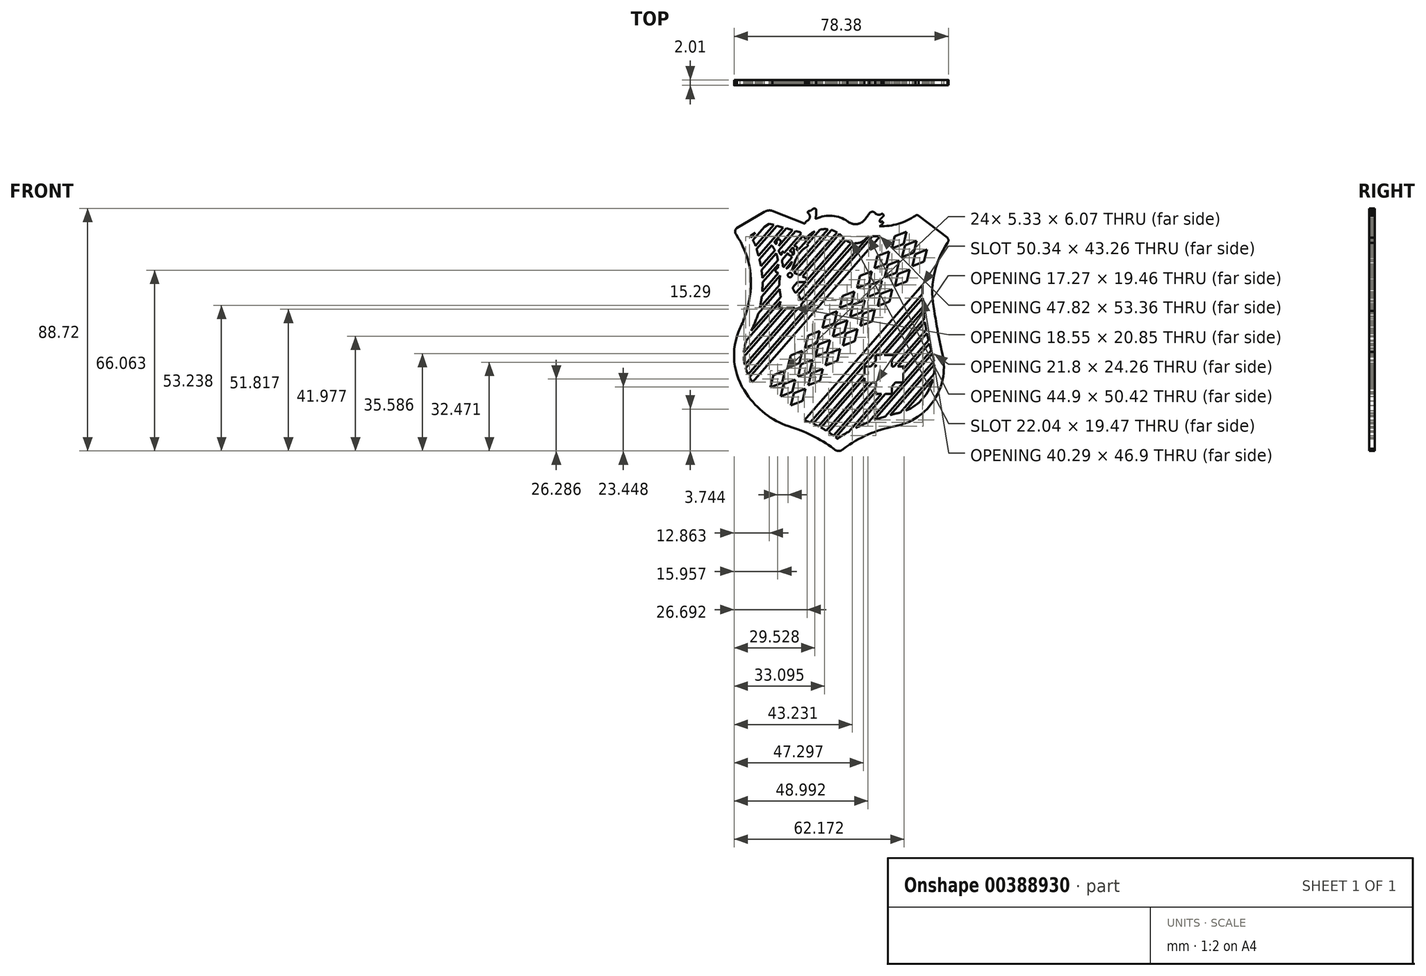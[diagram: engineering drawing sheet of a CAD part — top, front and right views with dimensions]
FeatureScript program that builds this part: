
annotation { "Feature Type Name" : "Feature", "Feature Type Description" : "" }
export const myFeature = defineFeature(function(context is Context, id is Id, definition is map)
    precondition{}
    {
        {
            var Q0;
            Q0=qCreatedBy(makeId("Front.planeOp"),FACE);
            var sketch = newSketch(context, id + "F0", { "sketchPlane" : qUnion([Q0])});
            skLineSegment(sketch, "E0", {"start": v(5.3, 4.8) * mm, "end": v(-12.55, -15.64) * mm});
            skLineSegment(sketch, "E1", {"start": v(11.24, -1.99) * mm, "end": v(-5.34, -20.97) * mm});
            skArc(sketch, "E2", {"start": v(-0.72, -23.55) * mm, "mid": v(-0.82, -23.46) * mm, "end": v(-0.92, -23.38) * mm});
            skArc(sketch, "E3", {"start": v(7.71, -19.98) * mm, "mid": v(7.22, -20.1) * mm, "end": v(6.72, -20.22) * mm});
            skArc(sketch, "E4", {"start": v(7.71, -19.98) * mm, "mid": v(7.92, -19.94) * mm, "end": v(8.13, -19.88) * mm});
            skArc(sketch, "E5", {"start": v(11.24, -1.99) * mm, "mid": v(11.23, -2.63) * mm, "end": v(11.23, -3.27) * mm});
            skArc(sketch, "E6", {"start": v(-11.88, 2.51) * mm, "mid": v(-11.95, 2.77) * mm, "end": v(-12.02, 3.03) * mm});
            skLineSegment(sketch, "E7", {"start": v(-10.25, 6.58) * mm, "end": v(-9.6, 6.4) * mm});
            skLineSegment(sketch, "E8", {"start": v(-5.95, 5.4) * mm, "end": v(-5.78, 5.19) * mm});
            skArc(sketch, "E9", {"start": v(0, 4.79) * mm, "mid": v(-0.2, 4.97) * mm, "end": v(-0.4, 5.14) * mm});
            skArc(sketch, "E10", {"start": v(0, 4.79) * mm, "mid": v(0.09, 4.66) * mm, "end": v(0.18, 4.54) * mm});
            skLineSegment(sketch, "E11", {"start": v(3.54, 4.79) * mm, "end": v(3.66, 4.79) * mm});
            skLineSegment(sketch, "E12", {"start": v(-10.08, -16.36) * mm, "end": v(-9.67, -14.67) * mm});
            skLineSegment(sketch, "E13", {"start": v(-9.67, -14.67) * mm, "end": v(-8.04, -14.03) * mm});
            skLineSegment(sketch, "E14", {"start": v(-8.45, -15.72) * mm, "end": v(-8.04, -14.03) * mm});
            skLineSegment(sketch, "E15", {"start": v(-10.08, -16.36) * mm, "end": v(-8.45, -15.72) * mm});
            skLineSegment(sketch, "E16", {"start": v(-7.65, -13.58) * mm, "end": v(-7.24, -11.89) * mm});
            skLineSegment(sketch, "E17", {"start": v(-7.24, -11.89) * mm, "end": v(-5.6, -11.25) * mm});
            skLineSegment(sketch, "E18", {"start": v(-6.02, -12.94) * mm, "end": v(-5.6, -11.25) * mm});
            skLineSegment(sketch, "E19", {"start": v(-7.65, -13.58) * mm, "end": v(-6.02, -12.94) * mm});
            skLineSegment(sketch, "E20", {"start": v(-5.22, -10.8) * mm, "end": v(-4.8, -9.1) * mm});
            skLineSegment(sketch, "E21", {"start": v(-4.8, -9.1) * mm, "end": v(-3.18, -8.47) * mm});
            skLineSegment(sketch, "E22", {"start": v(-3.58, -10.16) * mm, "end": v(-3.18, -8.47) * mm});
            skLineSegment(sketch, "E23", {"start": v(-5.22, -10.8) * mm, "end": v(-3.58, -10.16) * mm});
            skLineSegment(sketch, "E24", {"start": v(-2.79, -8) * mm, "end": v(-2.38, -6.32) * mm});
            skLineSegment(sketch, "E25", {"start": v(-2.38, -6.32) * mm, "end": v(-0.75, -5.68) * mm});
            skLineSegment(sketch, "E26", {"start": v(-1.15, -7.37) * mm, "end": v(-0.75, -5.68) * mm});
            skLineSegment(sketch, "E27", {"start": v(-2.79, -8) * mm, "end": v(-1.15, -7.37) * mm});
            skLineSegment(sketch, "E28", {"start": v(-0.36, -5.23) * mm, "end": v(0.05, -3.54) * mm});
            skLineSegment(sketch, "E29", {"start": v(0.05, -3.54) * mm, "end": v(1.69, -2.9) * mm});
            skLineSegment(sketch, "E30", {"start": v(1.28, -4.6) * mm, "end": v(1.69, -2.9) * mm});
            skLineSegment(sketch, "E31", {"start": v(-0.36, -5.23) * mm, "end": v(1.28, -4.6) * mm});
            skLineSegment(sketch, "E32", {"start": v(2.08, -2.44) * mm, "end": v(2.48, -0.75) * mm});
            skLineSegment(sketch, "E33", {"start": v(2.48, -0.75) * mm, "end": v(4.12, -0.12) * mm});
            skLineSegment(sketch, "E34", {"start": v(3.7, -1.8) * mm, "end": v(4.12, -0.12) * mm});
            skLineSegment(sketch, "E35", {"start": v(2.08, -2.44) * mm, "end": v(3.7, -1.8) * mm});
            skLineSegment(sketch, "E36", {"start": v(4.5, 0.34) * mm, "end": v(4.91, 2.03) * mm});
            skLineSegment(sketch, "E37", {"start": v(4.91, 2.03) * mm, "end": v(6.55, 2.67) * mm});
            skLineSegment(sketch, "E38", {"start": v(6.14, 0.98) * mm, "end": v(6.55, 2.67) * mm});
            skLineSegment(sketch, "E39", {"start": v(4.5, 0.34) * mm, "end": v(6.14, 0.98) * mm});
            skLineSegment(sketch, "E40", {"start": v(6.94, 3.12) * mm, "end": v(7.35, 4.81) * mm});
            skLineSegment(sketch, "E41", {"start": v(7.35, 4.81) * mm, "end": v(8.98, 5.45) * mm});
            skLineSegment(sketch, "E42", {"start": v(8.57, 3.76) * mm, "end": v(8.98, 5.45) * mm});
            skLineSegment(sketch, "E43", {"start": v(6.94, 3.12) * mm, "end": v(8.57, 3.76) * mm});
            skLineSegment(sketch, "E44", {"start": v(-8.64, -17.61) * mm, "end": v(-8.24, -15.92) * mm});
            skLineSegment(sketch, "E45", {"start": v(-8.24, -15.92) * mm, "end": v(-6.6, -15.29) * mm});
            skLineSegment(sketch, "E46", {"start": v(-7.01, -16.98) * mm, "end": v(-6.6, -15.29) * mm});
            skLineSegment(sketch, "E47", {"start": v(-8.64, -17.61) * mm, "end": v(-7.01, -16.98) * mm});
            skLineSegment(sketch, "E48", {"start": v(-6.21, -14.83) * mm, "end": v(-5.8, -13.14) * mm});
            skLineSegment(sketch, "E49", {"start": v(-5.8, -13.14) * mm, "end": v(-4.17, -12.5) * mm});
            skLineSegment(sketch, "E50", {"start": v(-4.58, -14.2) * mm, "end": v(-4.17, -12.5) * mm});
            skLineSegment(sketch, "E51", {"start": v(-6.21, -14.83) * mm, "end": v(-4.58, -14.2) * mm});
            skLineSegment(sketch, "E52", {"start": v(-3.78, -12.04) * mm, "end": v(-3.37, -10.36) * mm});
            skLineSegment(sketch, "E53", {"start": v(-3.37, -10.36) * mm, "end": v(-1.74, -9.72) * mm});
            skLineSegment(sketch, "E54", {"start": v(-2.15, -11.4) * mm, "end": v(-1.74, -9.72) * mm});
            skLineSegment(sketch, "E55", {"start": v(-3.78, -12.04) * mm, "end": v(-2.15, -11.4) * mm});
            skLineSegment(sketch, "E56", {"start": v(-1.35, -9.26) * mm, "end": v(-0.94, -7.57) * mm});
            skLineSegment(sketch, "E57", {"start": v(-0.94, -7.57) * mm, "end": v(0.69, -6.94) * mm});
            skLineSegment(sketch, "E58", {"start": v(0.28, -8.63) * mm, "end": v(0.69, -6.94) * mm});
            skLineSegment(sketch, "E59", {"start": v(-1.35, -9.26) * mm, "end": v(0.28, -8.63) * mm});
            skLineSegment(sketch, "E60", {"start": v(1.08, -6.48) * mm, "end": v(1.49, -4.79) * mm});
            skLineSegment(sketch, "E61", {"start": v(1.49, -4.79) * mm, "end": v(3.12, -4.15) * mm});
            skLineSegment(sketch, "E62", {"start": v(2.71, -5.84) * mm, "end": v(3.12, -4.15) * mm});
            skLineSegment(sketch, "E63", {"start": v(1.08, -6.48) * mm, "end": v(2.71, -5.84) * mm});
            skLineSegment(sketch, "E64", {"start": v(3.5, -3.7) * mm, "end": v(3.92, -2) * mm});
            skLineSegment(sketch, "E65", {"start": v(3.92, -2) * mm, "end": v(5.55, -1.37) * mm});
            skLineSegment(sketch, "E66", {"start": v(5.14, -3.06) * mm, "end": v(5.55, -1.37) * mm});
            skLineSegment(sketch, "E67", {"start": v(3.5, -3.7) * mm, "end": v(5.14, -3.06) * mm});
            skLineSegment(sketch, "E68", {"start": v(5.94, -0.91) * mm, "end": v(6.35, 0.78) * mm});
            skLineSegment(sketch, "E69", {"start": v(6.35, 0.78) * mm, "end": v(7.98, 1.41) * mm});
            skLineSegment(sketch, "E70", {"start": v(7.57, -0.28) * mm, "end": v(7.98, 1.41) * mm});
            skLineSegment(sketch, "E71", {"start": v(5.94, -0.91) * mm, "end": v(7.57, -0.28) * mm});
            skLineSegment(sketch, "E72", {"start": v(8.37, 1.87) * mm, "end": v(8.78, 3.56) * mm});
            skLineSegment(sketch, "E73", {"start": v(8.78, 3.56) * mm, "end": v(10.41, 4.2) * mm});
            skLineSegment(sketch, "E74", {"start": v(10, 2.5) * mm, "end": v(10.41, 4.2) * mm});
            skLineSegment(sketch, "E75", {"start": v(8.37, 1.87) * mm, "end": v(10, 2.5) * mm});
            skLineSegment(sketch, "E76", {"start": v(-7.21, -18.86) * mm, "end": v(-6.8, -17.17) * mm});
            skLineSegment(sketch, "E77", {"start": v(-6.8, -17.17) * mm, "end": v(-5.17, -16.54) * mm});
            skLineSegment(sketch, "E78", {"start": v(-5.58, -18.23) * mm, "end": v(-5.17, -16.54) * mm});
            skLineSegment(sketch, "E79", {"start": v(-7.21, -18.86) * mm, "end": v(-5.58, -18.23) * mm});
            skLineSegment(sketch, "E80", {"start": v(-4.78, -16.08) * mm, "end": v(-4.37, -14.4) * mm});
            skLineSegment(sketch, "E81", {"start": v(-4.37, -14.4) * mm, "end": v(-2.74, -13.76) * mm});
            skLineSegment(sketch, "E82", {"start": v(-3.15, -15.45) * mm, "end": v(-2.74, -13.76) * mm});
            skLineSegment(sketch, "E83", {"start": v(-4.78, -16.08) * mm, "end": v(-3.15, -15.45) * mm});
            skLineSegment(sketch, "E84", {"start": v(-2.35, -13.3) * mm, "end": v(-1.94, -11.6) * mm});
            skLineSegment(sketch, "E85", {"start": v(-1.94, -11.6) * mm, "end": v(-0.3, -10.97) * mm});
            skLineSegment(sketch, "E86", {"start": v(-0.72, -12.66) * mm, "end": v(-0.3, -10.97) * mm});
            skLineSegment(sketch, "E87", {"start": v(-2.35, -13.3) * mm, "end": v(-0.72, -12.66) * mm});
            skLineSegment(sketch, "E88", {"start": v(0.08, -10.51) * mm, "end": v(0.5, -8.82) * mm});
            skLineSegment(sketch, "E89", {"start": v(0.5, -8.82) * mm, "end": v(2.12, -8.19) * mm});
            skLineSegment(sketch, "E90", {"start": v(1.72, -9.88) * mm, "end": v(2.12, -8.19) * mm});
            skLineSegment(sketch, "E91", {"start": v(0.08, -10.51) * mm, "end": v(1.72, -9.88) * mm});
            skLineSegment(sketch, "E92", {"start": v(2.51, -7.73) * mm, "end": v(2.92, -6.04) * mm});
            skLineSegment(sketch, "E93", {"start": v(2.92, -6.04) * mm, "end": v(4.55, -5.4) * mm});
            skLineSegment(sketch, "E94", {"start": v(4.15, -7.1) * mm, "end": v(4.55, -5.4) * mm});
            skLineSegment(sketch, "E95", {"start": v(2.51, -7.73) * mm, "end": v(4.15, -7.1) * mm});
            skLineSegment(sketch, "E96", {"start": v(4.94, -4.95) * mm, "end": v(5.35, -3.26) * mm});
            skLineSegment(sketch, "E97", {"start": v(5.35, -3.26) * mm, "end": v(6.99, -2.62) * mm});
            skLineSegment(sketch, "E98", {"start": v(6.58, -4.31) * mm, "end": v(6.99, -2.62) * mm});
            skLineSegment(sketch, "E99", {"start": v(4.94, -4.95) * mm, "end": v(6.58, -4.31) * mm});
            skLineSegment(sketch, "E100", {"start": v(7.37, -2.16) * mm, "end": v(7.78, -0.47) * mm});
            skLineSegment(sketch, "E101", {"start": v(7.78, -0.47) * mm, "end": v(9.42, 0.16) * mm});
            skLineSegment(sketch, "E102", {"start": v(9, -1.53) * mm, "end": v(9.42, 0.16) * mm});
            skLineSegment(sketch, "E103", {"start": v(7.37, -2.16) * mm, "end": v(9, -1.53) * mm});
            skLineSegment(sketch, "E104", {"start": v(9.8, 0.62) * mm, "end": v(10.21, 2.3) * mm});
            skLineSegment(sketch, "E105", {"start": v(10.21, 2.3) * mm, "end": v(11.85, 2.94) * mm});
            skLineSegment(sketch, "E106", {"start": v(11.44, 1.25) * mm, "end": v(11.85, 2.94) * mm});
            skLineSegment(sketch, "E107", {"start": v(9.8, 0.62) * mm, "end": v(11.44, 1.25) * mm});
            skLineSegment(sketch, "E108", {"start": v(-4.5, -21.28) * mm, "end": v(11.23, -3.27) * mm});
            skLineSegment(sketch, "E109", {"start": v(11.25, -3.84) * mm, "end": v(-4.12, -21.44) * mm});
            skLineSegment(sketch, "E110", {"start": v(-1.92, -22.65) * mm, "end": v(4.17, -15.68) * mm});
            skLineSegment(sketch, "E111", {"start": v(3.69, -21.23) * mm, "end": v(8.54, -15.68) * mm});
            skLineSegment(sketch, "E112", {"start": v(4.47, -20.93) * mm, "end": v(12.59, -11.64) * mm});
            skLineSegment(sketch, "E113", {"start": v(6.03, -20.42) * mm, "end": v(12.82, -12.64) * mm});
            skLineSegment(sketch, "E114", {"start": v(6.72, -20.22) * mm, "end": v(12.88, -13.17) * mm});
            skLineSegment(sketch, "E115", {"start": v(8.13, -19.88) * mm, "end": v(12.84, -14.49) * mm});
            skLineSegment(sketch, "E116", {"start": v(8.87, -19.63) * mm, "end": v(12.69, -15.26) * mm});
            skArc(sketch, "E117", {"start": v(-4.5, -21.28) * mm, "mid": v(-4.92, -21.12) * mm, "end": v(-5.34, -20.97) * mm});
            skArc(sketch, "E118", {"start": v(-3.34, -21.81) * mm, "mid": v(-3.73, -21.62) * mm, "end": v(-4.12, -21.44) * mm});
            skArc(sketch, "E119", {"start": v(-2.25, -22.43) * mm, "mid": v(-2.61, -22.21) * mm, "end": v(-2.98, -22) * mm});
            skArc(sketch, "E120", {"start": v(-1.23, -23.14) * mm, "mid": v(-1.57, -22.89) * mm, "end": v(-1.92, -22.65) * mm});
            skArc(sketch, "E121", {"start": v(0.9, -22.57) * mm, "mid": v(0.08, -23.04) * mm, "end": v(-0.72, -23.55) * mm});
            skArc(sketch, "E122", {"start": v(3.69, -21.23) * mm, "mid": v(2.76, -21.63) * mm, "end": v(1.86, -22.06) * mm});
            skArc(sketch, "E123", {"start": v(8.87, -19.63) * mm, "mid": v(11.3, -17.9) * mm, "end": v(12.69, -15.26) * mm});
            skArc(sketch, "E124", {"start": v(12.84, -14.49) * mm, "mid": v(12.9, -13.83) * mm, "end": v(12.88, -13.17) * mm});
            skLineSegment(sketch, "E125", {"start": v(12.88, -13.17) * mm, "end": v(12.88, -13.17) * mm});
            skArc(sketch, "E126", {"start": v(12.19, -10.23) * mm, "mid": v(12.32, -10.72) * mm, "end": v(12.45, -11.2) * mm});
            skLineSegment(sketch, "E127", {"start": v(11.84, -8.76) * mm, "end": v(11.84, -8.76) * mm});
            skLineSegment(sketch, "E128", {"start": v(11.75, -8.27) * mm, "end": v(11.75, -8.27) * mm});
            skArc(sketch, "E129", {"start": v(11.57, -7.21) * mm, "mid": v(11.65, -7.75) * mm, "end": v(11.75, -8.27) * mm});
            skArc(sketch, "E130", {"start": v(11.36, -5.58) * mm, "mid": v(11.42, -6.14) * mm, "end": v(11.5, -6.7) * mm});
            skArc(sketch, "E131", {"start": v(11.25, -3.84) * mm, "mid": v(11.28, -4.44) * mm, "end": v(11.32, -5.03) * mm});
            skArc(sketch, "E132", {"start": v(11.84, -8.76) * mm, "mid": v(11.95, -9.27) * mm, "end": v(12.07, -9.77) * mm});
            skLineSegment(sketch, "E133.bottom", {"start": v(3.1, -13.45) * mm, "end": v(3.96, -13.45) * mm});
            skLineSegment(sketch, "E133.top", {"start": v(3.1, -15.68) * mm, "end": v(3.65, -15.68) * mm});
            skLineSegment(sketch, "E133.left", {"start": v(3.1, -13.45) * mm, "end": v(3.1, -14.45) * mm});
            skLineSegment(sketch, "E134.bottom", {"start": v(6.93, -11.85) * mm, "end": v(6.93, -11.92) * mm});
            skLineSegment(sketch, "E134.right", {"start": v(6.93, -17.3) * mm, "end": v(6.02, -17.3) * mm});
            skLineSegment(sketch, "E135", {"start": v(4.7, -15.68) * mm, "end": v(4.7, -16.34) * mm});
            skLineSegment(sketch, "E136", {"start": v(4.7, -13.45) * mm, "end": v(4.7, -13.45) * mm});
            skLineSegment(sketch, "E137", {"start": v(3.96, -13.45) * mm, "end": v(4.7, -12.61) * mm});
            skLineSegment(sketch, "E138", {"start": v(3.1, -15.05) * mm, "end": v(3.1, -15.68) * mm});
            skLineSegment(sketch, "E139", {"start": v(4.48, -13.45) * mm, "end": v(4.7, -13.45) * mm});
            skLineSegment(sketch, "E140", {"start": v(4.7, -15.68) * mm, "end": v(4.17, -15.68) * mm});
            skLineSegment(sketch, "E141", {"start": v(3.1, -15.05) * mm, "end": v(-2.98, -22) * mm});
            skLineSegment(sketch, "E142", {"start": v(3.1, -14.45) * mm, "end": v(-3.34, -21.81) * mm});
            skLineSegment(sketch, "E143", {"start": v(5.37, -11.85) * mm, "end": v(11.32, -5.03) * mm});
            skLineSegment(sketch, "E144", {"start": v(5.89, -11.85) * mm, "end": v(11.36, -5.58) * mm});
            skLineSegment(sketch, "E145", {"start": v(4.7, -13.2) * mm, "end": v(4.7, -13.45) * mm});
            skLineSegment(sketch, "E146", {"start": v(4.48, -13.45) * mm, "end": v(4.7, -13.2) * mm});
            skLineSegment(sketch, "E147", {"start": v(4.7, -12.61) * mm, "end": v(4.7, -11.85) * mm});
            skLineSegment(sketch, "E148", {"start": v(4.7, -11.85) * mm, "end": v(5.37, -11.85) * mm});
            skLineSegment(sketch, "E149", {"start": v(5.89, -11.85) * mm, "end": v(6.93, -11.85) * mm});
            skLineSegment(sketch, "E150", {"start": v(6.93, -12.52) * mm, "end": v(6.93, -13.45) * mm});
            skLineSegment(sketch, "E151", {"start": v(7.22, -13.45) * mm, "end": v(11.75, -8.27) * mm});
            skLineSegment(sketch, "E152", {"start": v(7.74, -13.45) * mm, "end": v(8.54, -13.45) * mm});
            skLineSegment(sketch, "E153", {"start": v(8.54, -13.82) * mm, "end": v(12.07, -9.77) * mm});
            skLineSegment(sketch, "E154", {"start": v(7.43, -15.68) * mm, "end": v(8.54, -15.68) * mm});
            skLineSegment(sketch, "E155", {"start": v(6.93, -16.25) * mm, "end": v(6.93, -17.3) * mm});
            skLineSegment(sketch, "E156", {"start": v(5.5, -17.3) * mm, "end": v(4.7, -17.3) * mm});
            skLineSegment(sketch, "E157", {"start": v(4.7, -16.94) * mm, "end": v(4.7, -17.3) * mm});
            skLineSegment(sketch, "E158", {"start": v(-1.23, -23.14) * mm, "end": v(4.7, -16.34) * mm});
            skLineSegment(sketch, "E159", {"start": v(4.7, -16.94) * mm, "end": v(-0.92, -23.38) * mm});
            skLineSegment(sketch, "E160", {"start": v(7.74, -13.45) * mm, "end": v(11.84, -8.76) * mm});
            skLineSegment(sketch, "E161", {"start": v(6.93, -13.45) * mm, "end": v(7.22, -13.45) * mm});
            skLineSegment(sketch, "E162", {"start": v(8.54, -13.45) * mm, "end": v(8.54, -13.82) * mm});
            skLineSegment(sketch, "E163", {"start": v(8.54, -14.41) * mm, "end": v(12.19, -10.23) * mm});
            skLineSegment(sketch, "E164", {"start": v(7.43, -15.68) * mm, "end": v(6.93, -16.25) * mm});
            skLineSegment(sketch, "E165", {"start": v(6.02, -17.3) * mm, "end": v(1.86, -22.06) * mm});
            skLineSegment(sketch, "E166", {"start": v(0.9, -22.57) * mm, "end": v(5.5, -17.3) * mm});
            skLineSegment(sketch, "E167", {"start": v(-2.25, -22.43) * mm, "end": v(3.65, -15.68) * mm});
            skLineSegment(sketch, "E168", {"start": v(6.93, -12.52) * mm, "end": v(11.57, -7.21) * mm});
            skLineSegment(sketch, "E169", {"start": v(11.5, -6.7) * mm, "end": v(6.93, -11.92) * mm});
            skLineSegment(sketch, "E170", {"start": v(-13.02, -14.92) * mm, "end": v(-13.02, -14.92) * mm});
            skLineSegment(sketch, "E171", {"start": v(-13.02, -14.92) * mm, "end": v(4.2, 4.8) * mm});
            skLineSegment(sketch, "E172", {"start": v(-13.22, -14.53) * mm, "end": v(3.66, 4.79) * mm});
            skLineSegment(sketch, "E173", {"start": v(-13.55, -13.65) * mm, "end": v(-13.55, -13.65) * mm});
            skArc(sketch, "E174", {"start": v(-13.55, -13.65) * mm, "mid": v(-13.4, -14.1) * mm, "end": v(-13.22, -14.53) * mm});
            skArc(sketch, "E175", {"start": v(-13.8, -12.07) * mm, "mid": v(-13.76, -12.63) * mm, "end": v(-13.67, -13.18) * mm});
            skArc(sketch, "E176", {"start": v(-13.44, -9.8) * mm, "mid": v(-13.67, -10.61) * mm, "end": v(-13.79, -11.45) * mm});
            skArc(sketch, "E177", {"start": v(-12.78, -8.43) * mm, "mid": v(-12.24, -7.27) * mm, "end": v(-11.8, -6.06) * mm});
            skLineSegment(sketch, "E178", {"start": v(-11.8, -6.06) * mm, "end": v(-11.8, -6.06) * mm});
            skArc(sketch, "E179", {"start": v(-11.56, -5.17) * mm, "mid": v(-11.4, -4.39) * mm, "end": v(-11.28, -3.6) * mm});
            skArc(sketch, "E180", {"start": v(-11.21, -2.9) * mm, "mid": v(-11.18, -2.26) * mm, "end": v(-11.18, -1.61) * mm});
            skLineSegment(sketch, "E181", {"start": v(-13.55, -13.65) * mm, "end": v(-6.16, -5.2) * mm});
            skLineSegment(sketch, "E182", {"start": v(-13.67, -13.18) * mm, "end": v(-6.69, -5.2) * mm});
            skLineSegment(sketch, "E183", {"start": v(-11.8, -6.06) * mm, "end": v(-8.79, -2.6) * mm});
            skLineSegment(sketch, "E184", {"start": v(-11.56, -5.17) * mm, "end": v(-8.82, -2.03) * mm});
            skLineSegment(sketch, "E185", {"start": v(-11.28, -3.6) * mm, "end": v(-8.74, -0.68) * mm});
            skPoint(sketch, "E185.endSnap0", {"position": v(-2.66, 5.8) * mm});
            skArc(sketch, "E186", {"start": v(-13.02, -14.92) * mm, "mid": v(-12.8, -15.28) * mm, "end": v(-12.55, -15.64) * mm});
            skLineSegment(sketch, "E187", {"start": v(4.2, 4.8) * mm, "end": v(5.3, 4.8) * mm});
            skArc(sketch, "E188", {"start": v(1.7, 3.82) * mm, "mid": v(2.76, 4.06) * mm, "end": v(3.54, 4.79) * mm});
            skArc(sketch, "E189", {"start": v(0.47, 4.27) * mm, "mid": v(0.84, 4.04) * mm, "end": v(1.24, 3.89) * mm});
            skArc(sketch, "E190", {"start": v(-0.73, 5.36) * mm, "mid": v(-1.12, 5.56) * mm, "end": v(-1.54, 5.7) * mm});
            skArc(sketch, "E191", {"start": v(-2, 5.79) * mm, "mid": v(-2.56, 5.81) * mm, "end": v(-3.13, 5.74) * mm});
            skLineSegment(sketch, "E192", {"start": v(-11.21, -2.9) * mm, "end": v(-8.97, -0.33) * mm});
            skArc(sketch, "E193", {"start": v(-3.89, 5.49) * mm, "mid": v(-4.58, 5.04) * mm, "end": v(-5.15, 4.44) * mm});
            skLineSegment(sketch, "E194", {"start": v(-11.18, -1.61) * mm, "end": v(-11.18, -1.61) * mm});
            skArc(sketch, "E195", {"start": v(-11.2, -1.03) * mm, "mid": v(-11.25, -0.47) * mm, "end": v(-11.32, 0.1) * mm});
            skLineSegment(sketch, "E196", {"start": v(-11.4, 0.6) * mm, "end": v(-11.4, 0.6) * mm});
            skLineSegment(sketch, "E197", {"start": v(-11.75, 2.08) * mm, "end": v(-11.75, 2.08) * mm});
            skLineSegment(sketch, "E198", {"start": v(-12.02, 3.03) * mm, "end": v(-12.02, 3.03) * mm});
            skArc(sketch, "E199", {"start": v(-12.16, 3.47) * mm, "mid": v(-12.34, 3.9) * mm, "end": v(-12.54, 4.3) * mm});
            skArc(sketch, "E200", {"start": v(-11.4, 0.6) * mm, "mid": v(-11.5, 1.11) * mm, "end": v(-11.62, 1.61) * mm});
            skArc(sketch, "E201", {"start": v(-11.75, 2.08) * mm, "mid": v(-11.82, 2.3) * mm, "end": v(-11.88, 2.51) * mm});
            skArc(sketch, "E202", {"start": v(-12.75, 4.66) * mm, "mid": v(-12.82, 4.76) * mm, "end": v(-12.88, 4.85) * mm});
            skLineSegment(sketch, "E203", {"start": v(-11.18, -1.61) * mm, "end": v(-9, 0.9) * mm});
            skLineSegment(sketch, "E204", {"start": v(-11.2, -1.03) * mm, "end": v(-9.03, 1.46) * mm});
            skLineSegment(sketch, "E205", {"start": v(-11.32, 0.1) * mm, "end": v(-9.27, 2.44) * mm});
            skLineSegment(sketch, "E206", {"start": v(-11.4, 0.6) * mm, "end": v(-9.45, 2.84) * mm});
            skLineSegment(sketch, "E207", {"start": v(-11.62, 1.61) * mm, "end": v(-9.92, 3.57) * mm});
            skLineSegment(sketch, "E208", {"start": v(-11.75, 2.08) * mm, "end": v(-8.29, 6.04) * mm});
            skLineSegment(sketch, "E209", {"start": v(-12.02, 3.03) * mm, "end": v(-9.17, 6.29) * mm});
            skLineSegment(sketch, "E210", {"start": v(-12.16, 3.47) * mm, "end": v(-9.6, 6.4) * mm});
            skLineSegment(sketch, "E211", {"start": v(-12.54, 4.3) * mm, "end": v(-10.94, 6.13) * mm});
            skLineSegment(sketch, "E212", {"start": v(-12.75, 4.66) * mm, "end": v(-12.2, 5.3) * mm});
            skLineSegment(sketch, "E213", {"start": v(-10.94, 6.13) * mm, "end": v(-10.25, 6.58) * mm});
            skLineSegment(sketch, "E214", {"start": v(-12.88, 4.85) * mm, "end": v(-12.2, 5.3) * mm});
            skLineSegment(sketch, "E215", {"start": v(-9.17, 6.29) * mm, "end": v(-8.29, 6.04) * mm});
            skLineSegment(sketch, "E216", {"start": v(-7.86, 5.92) * mm, "end": v(-6.97, 5.68) * mm});
            skLineSegment(sketch, "E217", {"start": v(-6.55, 5.56) * mm, "end": v(-5.95, 5.4) * mm});
            skLineSegment(sketch, "E218", {"start": v(-5.52, 4.88) * mm, "end": v(-5.15, 4.44) * mm});
            skArc(sketch, "E219", {"start": v(-14.78, 5.97) * mm, "mid": v(-15.02, 5.54) * mm, "end": v(-14.88, 5.06) * mm});
            skLineSegment(sketch, "E220", {"start": v(-14.78, 5.97) * mm, "end": v(-10.95, 8.24) * mm});
            skArc(sketch, "E221", {"start": v(-9.78, 8.38) * mm, "mid": v(-10.38, 8.43) * mm, "end": v(-10.95, 8.24) * mm});
            skArc(sketch, "E222", {"start": v(-4.87, 7) * mm, "mid": v(-4.55, 7.5) * mm, "end": v(-4.8, 8.06) * mm});
            skArc(sketch, "E223", {"start": v(-4.87, 7) * mm, "mid": v(-5.1, 6.84) * mm, "end": v(-5.23, 6.58) * mm});
            skLineSegment(sketch, "E224", {"start": v(-9.78, 8.38) * mm, "end": v(-5.23, 6.58) * mm});
            skArc(sketch, "E225", {"start": v(14.75, 3.9) * mm, "mid": v(14.86, 4.27) * mm, "end": v(14.72, 4.61) * mm});
            skArc(sketch, "E226", {"start": v(10.67, 7.7) * mm, "mid": v(10.45, 7.79) * mm, "end": v(10.23, 7.7) * mm});
            skLineSegment(sketch, "E227", {"start": v(10.67, 7.7) * mm, "end": v(14.72, 4.61) * mm});
            skArc(sketch, "E228", {"start": v(-13.06, -4.19) * mm, "mid": v(-13.03, 0.62) * mm, "end": v(-14.88, 5.06) * mm});
            skArc(sketch, "E229", {"start": v(-14.32, -8.04) * mm, "mid": v(-13.56, -6.16) * mm, "end": v(-13.06, -4.19) * mm});
            skArc(sketch, "E230", {"start": v(-14.32, -8.04) * mm, "mid": v(-15.13, -12.79) * mm, "end": v(-13.4, -17.28) * mm});
            skArc(sketch, "E231", {"start": v(-13.4, -17.28) * mm, "mid": v(-10.84, -20.03) * mm, "end": v(-7.53, -21.82) * mm});
            skArc(sketch, "E232", {"start": v(-1.23, -24.95) * mm, "mid": v(-4.24, -23.1) * mm, "end": v(-7.53, -21.82) * mm});
            skArc(sketch, "E233", {"start": v(-1.23, -24.95) * mm, "mid": v(-0.52, -25.27) * mm, "end": v(0.18, -24.95) * mm});
            skArc(sketch, "E234", {"start": v(7.34, -21.82) * mm, "mid": v(3.58, -22.97) * mm, "end": v(0.18, -24.95) * mm});
            skArc(sketch, "E235", {"start": v(14.75, 3.9) * mm, "mid": v(12.83, -0.68) * mm, "end": v(12.88, -5.65) * mm});
            skArc(sketch, "E236", {"start": v(7.34, -21.82) * mm, "mid": v(12.92, -18.04) * mm, "end": v(13.94, -11.38) * mm});
            skArc(sketch, "E237", {"start": v(12.88, -5.65) * mm, "mid": v(13.36, -8.53) * mm, "end": v(13.94, -11.38) * mm});
            skArc(sketch, "E238", {"start": v(-4.71, 8.34) * mm, "mid": v(-4.84, 8.22) * mm, "end": v(-4.8, 8.06) * mm});
            skArc(sketch, "E239", {"start": v(-4.71, 8.34) * mm, "mid": v(-4.4, 8.44) * mm, "end": v(-4.12, 8.64) * mm});
            skArc(sketch, "E240", {"start": v(-3.67, 8.4) * mm, "mid": v(-3.67, 8.53) * mm, "end": v(-3.74, 8.64) * mm});
            skLineSegment(sketch, "E241", {"start": v(-10.25, 6.58) * mm, "end": v(-10.25, 6.58) * mm});
            skLineSegment(sketch, "E242", {"start": v(-10.94, 6.13) * mm, "end": v(-10.94, 6.13) * mm});
            skArc(sketch, "E243", {"start": v(4.58, 8.08) * mm, "mid": v(4.15, 8.25) * mm, "end": v(3.76, 7.98) * mm});
            skArc(sketch, "E244", {"start": v(3.1, 7.11) * mm, "mid": v(3.44, 7.54) * mm, "end": v(3.76, 7.98) * mm});
            skArc(sketch, "E245", {"start": v(0.73, 6.93) * mm, "mid": v(1.5, 6.54) * mm, "end": v(2.36, 6.6) * mm});
            skArc(sketch, "E246", {"start": v(0.73, 6.93) * mm, "mid": v(-1.41, 7.68) * mm, "end": v(-3.65, 7.3) * mm});
            skArc(sketch, "E247", {"start": v(-3.73, 7.37) * mm, "mid": v(-3.73, 7.29) * mm, "end": v(-3.65, 7.3) * mm});
            skArc(sketch, "E248", {"start": v(-3.73, 7.37) * mm, "mid": v(-3.69, 7.73) * mm, "end": v(-3.67, 8.1) * mm});
            skLineSegment(sketch, "E249", {"start": v(-8.9, -5.2) * mm, "end": v(-8.32, -5.2) * mm});
            skArc(sketch, "E250", {"start": v(-5.83, -5.2) * mm, "mid": v(-5.78, -4.96) * mm, "end": v(-5.75, -4.73) * mm});
            skArc(sketch, "E251", {"start": v(-5.31, -1.6) * mm, "mid": v(-5.22, -1.58) * mm, "end": v(-5.14, -1.55) * mm});
            skArc(sketch, "E252", {"start": v(-4.97, -1.28) * mm, "mid": v(-5.09, -1.05) * mm, "end": v(-5.31, -0.9) * mm});
            skArc(sketch, "E253", {"start": v(-7, 0.27) * mm, "mid": v(-7.03, 0.18) * mm, "end": v(-7.06, 0.08) * mm});
            skLineSegment(sketch, "E254", {"start": v(-7, 0.27) * mm, "end": v(-6.51, 1.56) * mm});
            skArc(sketch, "E255", {"start": v(-5.04, 3.3) * mm, "mid": v(-5.37, 3.08) * mm, "end": v(-5.67, 2.83) * mm});
            skArc(sketch, "E256", {"start": v(-5.04, 3.3) * mm, "mid": v(-4.9, 3.39) * mm, "end": v(-4.82, 3.53) * mm});
            skArc(sketch, "E257", {"start": v(-4.82, 3.53) * mm, "mid": v(-4.84, 3.58) * mm, "end": v(-4.9, 3.6) * mm});
            skArc(sketch, "E258", {"start": v(-4.9, 3.6) * mm, "mid": v(-4.95, 3.6) * mm, "end": v(-5, 3.6) * mm});
            skArc(sketch, "E259", {"start": v(-6.23, 2.9) * mm, "mid": v(-6.1, 3.02) * mm, "end": v(-5.98, 3.14) * mm});
            skArc(sketch, "E260", {"start": v(-6.36, 2.9) * mm, "mid": v(-6.3, 2.87) * mm, "end": v(-6.23, 2.9) * mm});
            skArc(sketch, "E261", {"start": v(-6.36, 3.08) * mm, "mid": v(-6.38, 3) * mm, "end": v(-6.36, 2.9) * mm});
            skArc(sketch, "E262", {"start": v(-6.36, 3.08) * mm, "mid": v(-6.36, 3.3) * mm, "end": v(-6.53, 3.44) * mm});
            skArc(sketch, "E263", {"start": v(-6.53, 3.44) * mm, "mid": v(-6.65, 3.46) * mm, "end": v(-6.77, 3.43) * mm});
            skArc(sketch, "E264", {"start": v(-6.77, 2.95) * mm, "mid": v(-6.78, 3.04) * mm, "end": v(-6.84, 3.11) * mm});
            skLineSegment(sketch, "E265", {"start": v(-6.77, 2.95) * mm, "end": v(-6.77, 2.41) * mm});
            skArc(sketch, "E266", {"start": v(-6.96, 2.24) * mm, "mid": v(-6.83, 2.28) * mm, "end": v(-6.77, 2.41) * mm});
            skArc(sketch, "E267", {"start": v(-7, 2.3) * mm, "mid": v(-7, 2.27) * mm, "end": v(-6.96, 2.24) * mm});
            skArc(sketch, "E268", {"start": v(-7, 2.3) * mm, "mid": v(-7.04, 2.55) * mm, "end": v(-7.23, 2.7) * mm});
            skArc(sketch, "E269", {"start": v(-7.23, 2.7) * mm, "mid": v(-7.32, 2.72) * mm, "end": v(-7.41, 2.7) * mm});
            skArc(sketch, "E270", {"start": v(-7.59, 2.32) * mm, "mid": v(-7.53, 2.25) * mm, "end": v(-7.44, 2.2) * mm});
            skArc(sketch, "E271", {"start": v(-7.7, 0.34) * mm, "mid": v(-7.3, 0.73) * mm, "end": v(-7.06, 1.24) * mm});
            skArc(sketch, "E272", {"start": v(-8.34, 0.84) * mm, "mid": v(-8.32, 0.66) * mm, "end": v(-8.24, 0.5) * mm});
            skArc(sketch, "E273", {"start": v(-8.34, 0.84) * mm, "mid": v(-8.34, 0.9) * mm, "end": v(-8.37, 0.97) * mm});
            skArc(sketch, "E274", {"start": v(-8.27, 2.65) * mm, "mid": v(-8.44, 2.59) * mm, "end": v(-8.48, 2.41) * mm});
            skArc(sketch, "E275", {"start": v(-8.68, 2.3) * mm, "mid": v(-8.52, 2.26) * mm, "end": v(-8.48, 2.41) * mm});
            skArc(sketch, "E276", {"start": v(-8.64, 3.91) * mm, "mid": v(-8.77, 3.72) * mm, "end": v(-8.87, 3.51) * mm});
            skArc(sketch, "E277", {"start": v(-8.64, 3.91) * mm, "mid": v(-8.8, 4.34) * mm, "end": v(-9.22, 4.14) * mm});
            skArc(sketch, "E278", {"start": v(-9.22, 4.14) * mm, "mid": v(-9.24, 4.03) * mm, "end": v(-9.22, 3.91) * mm});
            skArc(sketch, "E279", {"start": v(-9.4, 3.87) * mm, "mid": v(-9.28, 3.77) * mm, "end": v(-9.22, 3.91) * mm});
            skArc(sketch, "E280", {"start": v(-9.4, 3.87) * mm, "mid": v(-9.45, 3.95) * mm, "end": v(-9.53, 4.02) * mm});
            skArc(sketch, "E281", {"start": v(-9, 0.5) * mm, "mid": v(-9, 0.7) * mm, "end": v(-9, 0.9) * mm});
            skArc(sketch, "E282", {"start": v(-9.14, 0.31) * mm, "mid": v(-9.05, 0.4) * mm, "end": v(-9, 0.5) * mm});
            skArc(sketch, "E283", {"start": v(-9.14, 0.31) * mm, "mid": v(-9.38, 0.02) * mm, "end": v(-9.14, -0.27) * mm});
            skArc(sketch, "E284", {"start": v(-8.75, -0.89) * mm, "mid": v(-8.73, -0.78) * mm, "end": v(-8.74, -0.68) * mm});
            skArc(sketch, "E285", {"start": v(-8.75, -0.89) * mm, "mid": v(-8.8, -1.46) * mm, "end": v(-8.82, -2.03) * mm});
            skArc(sketch, "E286", {"start": v(-8.9, -5.2) * mm, "mid": v(-8.76, -4.77) * mm, "end": v(-8.68, -4.34) * mm});
            skArc(sketch, "E287", {"start": v(-8.65, -3.7) * mm, "mid": v(-8.66, -3.51) * mm, "end": v(-8.68, -3.33) * mm});
            skArc(sketch, "E288", {"start": v(-6.94, -2.36) * mm, "mid": v(-6.8, -2.78) * mm, "end": v(-6.52, -3.13) * mm});
            skLineSegment(sketch, "E289", {"start": v(-13.44, -9.8) * mm, "end": v(-8.68, -4.34) * mm});
            skLineSegment(sketch, "E290", {"start": v(-6.94, -2.36) * mm, "end": v(-6.28, -1.6) * mm});
            skLineSegment(sketch, "E291", {"start": v(-12.78, -8.43) * mm, "end": v(-8.65, -3.7) * mm});
            skLineSegment(sketch, "E292", {"start": v(-7.79, -5.2) * mm, "end": v(-6.69, -5.2) * mm});
            skArc(sketch, "E293", {"start": v(-5.14, -1.55) * mm, "mid": v(-5.02, -1.44) * mm, "end": v(-4.97, -1.28) * mm});
            skLineSegment(sketch, "E294", {"start": v(-5, -1.39) * mm, "end": v(0.18, 4.54) * mm});
            skLineSegment(sketch, "E295", {"start": v(-13.79, -11.45) * mm, "end": v(-8.32, -5.2) * mm});
            skLineSegment(sketch, "E296", {"start": v(-13.8, -12.07) * mm, "end": v(-7.79, -5.2) * mm});
            skLineSegment(sketch, "E297", {"start": v(-6.22, -3.4) * mm, "end": v(0.47, 4.27) * mm});
            skLineSegment(sketch, "E298", {"start": v(-5.75, -4.73) * mm, "end": v(-5.75, -4.73) * mm});
            skArc(sketch, "E299", {"start": v(-5.8, -4.18) * mm, "mid": v(-5.97, -3.76) * mm, "end": v(-6.22, -3.4) * mm});
            skLineSegment(sketch, "E300", {"start": v(1.24, 3.89) * mm, "end": v(-5.8, -4.18) * mm});
            skLineSegment(sketch, "E301", {"start": v(-6.52, -3.13) * mm, "end": v(-5.14, -1.55) * mm});
            skLineSegment(sketch, "E302", {"start": v(-5.58, -0.8) * mm, "end": v(-0.4, 5.14) * mm});
            skArc(sketch, "E303", {"start": v(-8.79, -2.6) * mm, "mid": v(-8.74, -2.97) * mm, "end": v(-8.68, -3.33) * mm});
            skLineSegment(sketch, "E304", {"start": v(-7.06, -0.02) * mm, "end": v(-2, 5.79) * mm});
            skLineSegment(sketch, "E305", {"start": v(-6.76, -0.29) * mm, "end": v(-1.54, 5.7) * mm});
            skLineSegment(sketch, "E306", {"start": v(-0.73, 5.36) * mm, "end": v(-5.96, -0.63) * mm});
            skCircle(sketch, "E307", {"center": v(-7.34, -0.62) * mm, "radius": 0.3 * mm});
            skLineSegment(sketch, "E308", {"start": v(-7.87, 0.31) * mm, "end": v(-7.87, 0.31) * mm});
            skLineSegment(sketch, "E309", {"start": v(-8.24, 0.5) * mm, "end": v(-8.24, 0.5) * mm});
            skArc(sketch, "E310", {"start": v(-7.06, 1.85) * mm, "mid": v(-7.22, 2.07) * mm, "end": v(-7.44, 2.2) * mm});
            skLineSegment(sketch, "E311", {"start": v(-6.1, 2.34) * mm, "end": v(-5.67, 2.83) * mm});
            skLineSegment(sketch, "E312", {"start": v(-5.67, 2.83) * mm, "end": v(-5.67, 2.83) * mm});
            skLineSegment(sketch, "E313", {"start": v(-5, 3.6) * mm, "end": v(-3.13, 5.74) * mm});
            skArc(sketch, "E314", {"start": v(-5.79, 3.3) * mm, "mid": v(-5.89, 3.23) * mm, "end": v(-5.98, 3.14) * mm});
            skLineSegment(sketch, "E315", {"start": v(-5.79, 3.3) * mm, "end": v(-5.79, 3.3) * mm});
            skArc(sketch, "E316", {"start": v(-6.93, 3.25) * mm, "mid": v(-6.9, 3.17) * mm, "end": v(-6.84, 3.11) * mm});
            skLineSegment(sketch, "E317", {"start": v(-6.77, 3.43) * mm, "end": v(-5.52, 4.88) * mm});
            skLineSegment(sketch, "E318", {"start": v(-7.41, 2.7) * mm, "end": v(-6.93, 3.25) * mm});
            skLineSegment(sketch, "E319", {"start": v(-9.53, 4.02) * mm, "end": v(-7.86, 5.92) * mm});
            skArc(sketch, "E320", {"start": v(-9.45, 2.84) * mm, "mid": v(-9.64, 3.18) * mm, "end": v(-9.85, 3.5) * mm});
            skLineSegment(sketch, "E321", {"start": v(-8.87, 3.51) * mm, "end": v(-6.97, 5.68) * mm});
            skLineSegment(sketch, "E322", {"start": v(-8.92, 2.84) * mm, "end": v(-6.55, 5.56) * mm});
            skArc(sketch, "E323", {"start": v(-8.44, 1.52) * mm, "mid": v(-8.45, 1.24) * mm, "end": v(-8.37, 0.97) * mm});
            skLineSegment(sketch, "E324", {"start": v(-9.03, 1.46) * mm, "end": v(-9.03, 1.46) * mm});
            skArc(sketch, "E325", {"start": v(-8.15, 2.47) * mm, "mid": v(-8.2, 2.57) * mm, "end": v(-8.27, 2.65) * mm});
            skArc(sketch, "E326", {"start": v(-9.03, 1.46) * mm, "mid": v(-9.12, 1.96) * mm, "end": v(-9.27, 2.44) * mm});
            skLineSegment(sketch, "E327", {"start": v(-8.15, 2.47) * mm, "end": v(-5.78, 5.19) * mm});
            skLineSegment(sketch, "E328", {"start": v(-8.44, 1.52) * mm, "end": v(-7.6, 2.49) * mm});
            skArc(sketch, "E329", {"start": v(4.58, 8.08) * mm, "mid": v(5.02, 7.84) * mm, "end": v(5.5, 7.95) * mm});
            skArc(sketch, "E330", {"start": v(5.65, 6.6) * mm, "mid": v(5.67, 6.83) * mm, "end": v(5.44, 6.85) * mm});
            skArc(sketch, "E331", {"start": v(5.76, 7.68) * mm, "mid": v(5.77, 7.76) * mm, "end": v(5.76, 7.83) * mm});
            skArc(sketch, "E332", {"start": v(5.23, 7) * mm, "mid": v(5.28, 6.84) * mm, "end": v(5.44, 6.85) * mm});
            skArc(sketch, "E333", {"start": v(5.76, 7.83) * mm, "mid": v(5.65, 7.94) * mm, "end": v(5.5, 7.95) * mm});
            skLineSegment(sketch, "E334", {"start": v(5.44, 6.85) * mm, "end": v(5.44, 6.85) * mm});
            skLineSegment(sketch, "E335", {"start": v(5.65, 6.6) * mm, "end": v(5.65, 6.6) * mm});
            skArc(sketch, "E336", {"start": v(5.5, 7.4) * mm, "mid": v(5.34, 7.22) * mm, "end": v(5.23, 7) * mm});
            skArc(sketch, "E337", {"start": v(5.5, 7.4) * mm, "mid": v(5.65, 7.52) * mm, "end": v(5.76, 7.68) * mm});
            skArc(sketch, "E338", {"start": v(5.2, 6.22) * mm, "mid": v(5.21, 6.23) * mm, "end": v(5.22, 6.23) * mm});
            skArc(sketch, "E339", {"start": v(5.22, 6.23) * mm, "mid": v(5.46, 6.4) * mm, "end": v(5.65, 6.6) * mm});
            skArc(sketch, "E340", {"start": v(5.22, 6.22) * mm, "mid": v(7.84, 6.57) * mm, "end": v(10.23, 7.7) * mm});
            skLineSegment(sketch, "E341", {"start": v(5.22, 6.22) * mm, "end": v(5.2, 6.22) * mm});
            skLineSegment(sketch, "E342", {"start": v(4.47, -20.93) * mm, "end": v(6.03, -20.42) * mm});
            skArc(sketch, "E343", {"start": v(12.82, -12.64) * mm, "mid": v(12.74, -12.13) * mm, "end": v(12.59, -11.64) * mm});
            skLineSegment(sketch, "E344", {"start": v(-3.67, 8.1) * mm, "end": v(-3.67, 8.1) * mm});
            skArc(sketch, "E345", {"start": v(-3.67, 8.1) * mm, "mid": v(-3.67, 8.25) * mm, "end": v(-3.67, 8.4) * mm});
            skLineSegment(sketch, "E346", {"start": v(2.36, 6.6) * mm, "end": v(2.36, 6.6) * mm});
            skArc(sketch, "E347", {"start": v(2.36, 6.6) * mm, "mid": v(2.76, 6.8) * mm, "end": v(3.1, 7.11) * mm});
            skLineSegment(sketch, "E348", {"start": v(-2.35, 15.33) * mm, "end": v(-2.35, 15.33) * mm});
            skLineSegment(sketch, "E349", {"start": v(1.96, 15.5) * mm, "end": v(1.96, 15.5) * mm});
            skArc(sketch, "E350", {"start": v(-3.74, 8.64) * mm, "mid": v(-3.93, 8.73) * mm, "end": v(-4.12, 8.64) * mm});
            skLineSegment(sketch, "E351", {"start": v(-5.31, -1.6) * mm, "end": v(-6.28, -1.6) * mm});
            skLineSegment(sketch, "E352", {"start": v(-5.31, -0.9) * mm, "end": v(-5.58, -0.8) * mm});
            skLineSegment(sketch, "E353", {"start": v(-5.96, -0.63) * mm, "end": v(-6.76, -0.29) * mm});
            skLineSegment(sketch, "E354", {"start": v(-5.75, -4.73) * mm, "end": v(1.7, 3.82) * mm});
            skLineSegment(sketch, "E355", {"start": v(-6.16, -5.2) * mm, "end": v(-5.83, -5.2) * mm});
            skLineSegment(sketch, "E356", {"start": v(-5.79, 3.3) * mm, "end": v(-3.89, 5.49) * mm});
            skArc(sketch, "E357", {"start": v(-6.1, 2.34) * mm, "mid": v(-6.33, 1.97) * mm, "end": v(-6.51, 1.56) * mm});
            skLineSegment(sketch, "E358", {"start": v(-8.24, 0.5) * mm, "end": v(-7.06, 1.85) * mm});
            skLineSegment(sketch, "E359", {"start": v(-7.87, 0.31) * mm, "end": v(-7.06, 1.24) * mm});
            skArc(sketch, "E360", {"start": v(-8.97, -0.33) * mm, "mid": v(-9.05, -0.3) * mm, "end": v(-9.14, -0.27) * mm});
            skArc(sketch, "E361", {"start": v(-7.87, 0.31) * mm, "mid": v(-7.79, 0.32) * mm, "end": v(-7.7, 0.34) * mm});
            skLineSegment(sketch, "E362", {"start": v(-8.82, -2.03) * mm, "end": v(-8.82, -2.03) * mm});
            skLineSegment(sketch, "E363", {"start": v(-7.06, 0.08) * mm, "end": v(-7.06, -0.02) * mm});
            skArc(sketch, "E364", {"start": v(-8.92, 2.84) * mm, "mid": v(-8.83, 2.55) * mm, "end": v(-8.68, 2.3) * mm});
            skArc(sketch, "E365", {"start": v(-9.92, 3.57) * mm, "mid": v(-9.89, 3.53) * mm, "end": v(-9.85, 3.5) * mm});
            skLineSegment(sketch, "E366", {"start": v(-7.6, 2.49) * mm, "end": v(-7.6, 2.49) * mm});
            skArc(sketch, "E367", {"start": v(-7.6, 2.49) * mm, "mid": v(-7.6, 2.4) * mm, "end": v(-7.59, 2.32) * mm});
            skArc(sketch, "E368", {"start": v(-7.52, 2.63) * mm, "mid": v(-7.57, 2.57) * mm, "end": v(-7.6, 2.49) * mm});
            skLineSegment(sketch, "E369", {"start": v(8.55, -15.67) * mm, "end": v(12.45, -11.2) * mm});
            skLineSegment(sketch, "E370", {"start": v(8.54, -14.41) * mm, "end": v(8.55, -15.67) * mm});
            skSolve(sketch);
        }
        {
            var Q0;
            Q0=makeQuery(id+"F0.imprint","IMPRINT",FACE,{"disambiguationData":[TD([[makeQuery(id+"F0.imprint","IMPRINT",EDGE,{"derivedFrom":sQuery(id+"F0.wireOp",EDGE,"E0")}),1.0]])]});
            extrude(context, id + "F1", {"entities" : qUnion([Q0]), "depth" : 0.77 * mm});
        }
        {
            var Q0;
            Q0=makeQuery(id+"F1.opExtrude","SWEPT_BODY",BODY,{"disambiguationData":[OSD([sQuery(id+"F0.wireOp",EDGE,"E0"),sQuery(id+"F0.wireOp",EDGE,"E1"),sQuery(id+"F0.wireOp",EDGE,"E2"),sQuery(id+"F0.wireOp",EDGE,"E3"),sQuery(id+"F0.wireOp",EDGE,"E4"),sQuery(id+"F0.wireOp",EDGE,"E5"),sQuery(id+"F0.wireOp",EDGE,"E6"),sQuery(id+"F0.wireOp",EDGE,"E7"),sQuery(id+"F0.wireOp",EDGE,"E8"),sQuery(id+"F0.wireOp",EDGE,"E9"),sQuery(id+"F0.wireOp",EDGE,"E10"),sQuery(id+"F0.wireOp",EDGE,"E11"),sQuery(id+"F0.wireOp",EDGE,"E12"),sQuery(id+"F0.wireOp",EDGE,"E13"),sQuery(id+"F0.wireOp",EDGE,"E14"),sQuery(id+"F0.wireOp",EDGE,"E15"),sQuery(id+"F0.wireOp",EDGE,"E16"),sQuery(id+"F0.wireOp",EDGE,"E17"),sQuery(id+"F0.wireOp",EDGE,"E18"),sQuery(id+"F0.wireOp",EDGE,"E19"),sQuery(id+"F0.wireOp",EDGE,"E20"),sQuery(id+"F0.wireOp",EDGE,"E21"),sQuery(id+"F0.wireOp",EDGE,"E22"),sQuery(id+"F0.wireOp",EDGE,"E23"),sQuery(id+"F0.wireOp",EDGE,"E24"),sQuery(id+"F0.wireOp",EDGE,"E25"),sQuery(id+"F0.wireOp",EDGE,"E26"),sQuery(id+"F0.wireOp",EDGE,"E27"),sQuery(id+"F0.wireOp",EDGE,"E28"),sQuery(id+"F0.wireOp",EDGE,"E29"),sQuery(id+"F0.wireOp",EDGE,"E30"),sQuery(id+"F0.wireOp",EDGE,"E31"),sQuery(id+"F0.wireOp",EDGE,"E32"),sQuery(id+"F0.wireOp",EDGE,"E33"),sQuery(id+"F0.wireOp",EDGE,"E34"),sQuery(id+"F0.wireOp",EDGE,"E35"),sQuery(id+"F0.wireOp",EDGE,"E36"),sQuery(id+"F0.wireOp",EDGE,"E37"),sQuery(id+"F0.wireOp",EDGE,"E38"),sQuery(id+"F0.wireOp",EDGE,"E39"),sQuery(id+"F0.wireOp",EDGE,"E40"),sQuery(id+"F0.wireOp",EDGE,"E41"),sQuery(id+"F0.wireOp",EDGE,"E42"),sQuery(id+"F0.wireOp",EDGE,"E43"),sQuery(id+"F0.wireOp",EDGE,"E44"),sQuery(id+"F0.wireOp",EDGE,"E45"),sQuery(id+"F0.wireOp",EDGE,"E46"),sQuery(id+"F0.wireOp",EDGE,"E47"),sQuery(id+"F0.wireOp",EDGE,"E48"),sQuery(id+"F0.wireOp",EDGE,"E49"),sQuery(id+"F0.wireOp",EDGE,"E50"),sQuery(id+"F0.wireOp",EDGE,"E51"),sQuery(id+"F0.wireOp",EDGE,"E52"),sQuery(id+"F0.wireOp",EDGE,"E53"),sQuery(id+"F0.wireOp",EDGE,"E54"),sQuery(id+"F0.wireOp",EDGE,"E55"),sQuery(id+"F0.wireOp",EDGE,"E56"),sQuery(id+"F0.wireOp",EDGE,"E57"),sQuery(id+"F0.wireOp",EDGE,"E58"),sQuery(id+"F0.wireOp",EDGE,"E59"),sQuery(id+"F0.wireOp",EDGE,"E60"),sQuery(id+"F0.wireOp",EDGE,"E61"),sQuery(id+"F0.wireOp",EDGE,"E62"),sQuery(id+"F0.wireOp",EDGE,"E63"),sQuery(id+"F0.wireOp",EDGE,"E64"),sQuery(id+"F0.wireOp",EDGE,"E65"),sQuery(id+"F0.wireOp",EDGE,"E66"),sQuery(id+"F0.wireOp",EDGE,"E67"),sQuery(id+"F0.wireOp",EDGE,"E68"),sQuery(id+"F0.wireOp",EDGE,"E69"),sQuery(id+"F0.wireOp",EDGE,"E70"),sQuery(id+"F0.wireOp",EDGE,"E71"),sQuery(id+"F0.wireOp",EDGE,"E72"),sQuery(id+"F0.wireOp",EDGE,"E73"),sQuery(id+"F0.wireOp",EDGE,"E74"),sQuery(id+"F0.wireOp",EDGE,"E75"),sQuery(id+"F0.wireOp",EDGE,"E76"),sQuery(id+"F0.wireOp",EDGE,"E77"),sQuery(id+"F0.wireOp",EDGE,"E78"),sQuery(id+"F0.wireOp",EDGE,"E79"),sQuery(id+"F0.wireOp",EDGE,"E80"),sQuery(id+"F0.wireOp",EDGE,"E81"),sQuery(id+"F0.wireOp",EDGE,"E82"),sQuery(id+"F0.wireOp",EDGE,"E83"),sQuery(id+"F0.wireOp",EDGE,"E84"),sQuery(id+"F0.wireOp",EDGE,"E85"),sQuery(id+"F0.wireOp",EDGE,"E86"),sQuery(id+"F0.wireOp",EDGE,"E87"),sQuery(id+"F0.wireOp",EDGE,"E88"),sQuery(id+"F0.wireOp",EDGE,"E89"),sQuery(id+"F0.wireOp",EDGE,"E90"),sQuery(id+"F0.wireOp",EDGE,"E91"),sQuery(id+"F0.wireOp",EDGE,"E92"),sQuery(id+"F0.wireOp",EDGE,"E93"),sQuery(id+"F0.wireOp",EDGE,"E94"),sQuery(id+"F0.wireOp",EDGE,"E95"),sQuery(id+"F0.wireOp",EDGE,"E96"),sQuery(id+"F0.wireOp",EDGE,"E97"),sQuery(id+"F0.wireOp",EDGE,"E98"),sQuery(id+"F0.wireOp",EDGE,"E99"),sQuery(id+"F0.wireOp",EDGE,"E100"),sQuery(id+"F0.wireOp",EDGE,"E101"),sQuery(id+"F0.wireOp",EDGE,"E102"),sQuery(id+"F0.wireOp",EDGE,"E103"),sQuery(id+"F0.wireOp",EDGE,"E104"),sQuery(id+"F0.wireOp",EDGE,"E105"),sQuery(id+"F0.wireOp",EDGE,"E106"),sQuery(id+"F0.wireOp",EDGE,"E107"),sQuery(id+"F0.wireOp",EDGE,"E108"),sQuery(id+"F0.wireOp",EDGE,"E109"),sQuery(id+"F0.wireOp",EDGE,"E110"),sQuery(id+"F0.wireOp",EDGE,"E111"),sQuery(id+"F0.wireOp",EDGE,"E112"),sQuery(id+"F0.wireOp",EDGE,"E113"),sQuery(id+"F0.wireOp",EDGE,"E114"),sQuery(id+"F0.wireOp",EDGE,"E115"),sQuery(id+"F0.wireOp",EDGE,"E116"),sQuery(id+"F0.wireOp",EDGE,"E117"),sQuery(id+"F0.wireOp",EDGE,"E118"),sQuery(id+"F0.wireOp",EDGE,"E119"),sQuery(id+"F0.wireOp",EDGE,"E120"),sQuery(id+"F0.wireOp",EDGE,"E121"),sQuery(id+"F0.wireOp",EDGE,"E122"),sQuery(id+"F0.wireOp",EDGE,"E123"),sQuery(id+"F0.wireOp",EDGE,"E124"),sQuery(id+"F0.wireOp",EDGE,"E126"),sQuery(id+"F0.wireOp",EDGE,"E129"),sQuery(id+"F0.wireOp",EDGE,"E130"),sQuery(id+"F0.wireOp",EDGE,"E131"),sQuery(id+"F0.wireOp",EDGE,"E132"),sQuery(id+"F0.wireOp",EDGE,"E133.bottom"),sQuery(id+"F0.wireOp",EDGE,"E133.top"),sQuery(id+"F0.wireOp",EDGE,"E133.left"),sQuery(id+"F0.wireOp",EDGE,"E134.bottom"),sQuery(id+"F0.wireOp",EDGE,"E134.right"),sQuery(id+"F0.wireOp",EDGE,"E135"),sQuery(id+"F0.wireOp",EDGE,"E137"),sQuery(id+"F0.wireOp",EDGE,"E138"),sQuery(id+"F0.wireOp",EDGE,"E139"),sQuery(id+"F0.wireOp",EDGE,"E140"),sQuery(id+"F0.wireOp",EDGE,"E141"),sQuery(id+"F0.wireOp",EDGE,"E142"),sQuery(id+"F0.wireOp",EDGE,"E143"),sQuery(id+"F0.wireOp",EDGE,"E144"),sQuery(id+"F0.wireOp",EDGE,"E145"),sQuery(id+"F0.wireOp",EDGE,"E146"),sQuery(id+"F0.wireOp",EDGE,"E147"),sQuery(id+"F0.wireOp",EDGE,"E148"),sQuery(id+"F0.wireOp",EDGE,"E149"),sQuery(id+"F0.wireOp",EDGE,"E150"),sQuery(id+"F0.wireOp",EDGE,"E151"),sQuery(id+"F0.wireOp",EDGE,"E152"),sQuery(id+"F0.wireOp",EDGE,"E153"),sQuery(id+"F0.wireOp",EDGE,"E154"),sQuery(id+"F0.wireOp",EDGE,"E155"),sQuery(id+"F0.wireOp",EDGE,"E156"),sQuery(id+"F0.wireOp",EDGE,"E157"),sQuery(id+"F0.wireOp",EDGE,"E158"),sQuery(id+"F0.wireOp",EDGE,"E159"),sQuery(id+"F0.wireOp",EDGE,"E160"),sQuery(id+"F0.wireOp",EDGE,"E161"),sQuery(id+"F0.wireOp",EDGE,"E162"),sQuery(id+"F0.wireOp",EDGE,"E163"),sQuery(id+"F0.wireOp",EDGE,"E164"),sQuery(id+"F0.wireOp",EDGE,"E165"),sQuery(id+"F0.wireOp",EDGE,"E166"),sQuery(id+"F0.wireOp",EDGE,"E167"),sQuery(id+"F0.wireOp",EDGE,"E168"),sQuery(id+"F0.wireOp",EDGE,"E169"),sQuery(id+"F0.wireOp",EDGE,"E171"),sQuery(id+"F0.wireOp",EDGE,"E172"),sQuery(id+"F0.wireOp",EDGE,"E174"),sQuery(id+"F0.wireOp",EDGE,"E175"),sQuery(id+"F0.wireOp",EDGE,"E176"),sQuery(id+"F0.wireOp",EDGE,"E177"),sQuery(id+"F0.wireOp",EDGE,"E179"),sQuery(id+"F0.wireOp",EDGE,"E180"),sQuery(id+"F0.wireOp",EDGE,"E181"),sQuery(id+"F0.wireOp",EDGE,"E182"),sQuery(id+"F0.wireOp",EDGE,"E183"),sQuery(id+"F0.wireOp",EDGE,"E184"),sQuery(id+"F0.wireOp",EDGE,"E185"),sQuery(id+"F0.wireOp",EDGE,"E186"),sQuery(id+"F0.wireOp",EDGE,"E187"),sQuery(id+"F0.wireOp",EDGE,"E188"),sQuery(id+"F0.wireOp",EDGE,"E189"),sQuery(id+"F0.wireOp",EDGE,"E190"),sQuery(id+"F0.wireOp",EDGE,"E191"),sQuery(id+"F0.wireOp",EDGE,"E192"),sQuery(id+"F0.wireOp",EDGE,"E193"),sQuery(id+"F0.wireOp",EDGE,"E195"),sQuery(id+"F0.wireOp",EDGE,"E199"),sQuery(id+"F0.wireOp",EDGE,"E200"),sQuery(id+"F0.wireOp",EDGE,"E201"),sQuery(id+"F0.wireOp",EDGE,"E202"),sQuery(id+"F0.wireOp",EDGE,"E203"),sQuery(id+"F0.wireOp",EDGE,"E204"),sQuery(id+"F0.wireOp",EDGE,"E205"),sQuery(id+"F0.wireOp",EDGE,"E206"),sQuery(id+"F0.wireOp",EDGE,"E207"),sQuery(id+"F0.wireOp",EDGE,"E208"),sQuery(id+"F0.wireOp",EDGE,"E209"),sQuery(id+"F0.wireOp",EDGE,"E210"),sQuery(id+"F0.wireOp",EDGE,"E211"),sQuery(id+"F0.wireOp",EDGE,"E212"),sQuery(id+"F0.wireOp",EDGE,"E213"),sQuery(id+"F0.wireOp",EDGE,"E214"),sQuery(id+"F0.wireOp",EDGE,"E215"),sQuery(id+"F0.wireOp",EDGE,"E216"),sQuery(id+"F0.wireOp",EDGE,"E217"),sQuery(id+"F0.wireOp",EDGE,"E218"),sQuery(id+"F0.wireOp",EDGE,"E219"),sQuery(id+"F0.wireOp",EDGE,"E220"),sQuery(id+"F0.wireOp",EDGE,"E221"),sQuery(id+"F0.wireOp",EDGE,"E222"),sQuery(id+"F0.wireOp",EDGE,"E223"),sQuery(id+"F0.wireOp",EDGE,"E224"),sQuery(id+"F0.wireOp",EDGE,"E225"),sQuery(id+"F0.wireOp",EDGE,"E226"),sQuery(id+"F0.wireOp",EDGE,"E227"),sQuery(id+"F0.wireOp",EDGE,"E228"),sQuery(id+"F0.wireOp",EDGE,"E229"),sQuery(id+"F0.wireOp",EDGE,"E230"),sQuery(id+"F0.wireOp",EDGE,"E231"),sQuery(id+"F0.wireOp",EDGE,"E232"),sQuery(id+"F0.wireOp",EDGE,"E233"),sQuery(id+"F0.wireOp",EDGE,"E234"),sQuery(id+"F0.wireOp",EDGE,"E235"),sQuery(id+"F0.wireOp",EDGE,"E236"),sQuery(id+"F0.wireOp",EDGE,"E237"),sQuery(id+"F0.wireOp",EDGE,"E238"),sQuery(id+"F0.wireOp",EDGE,"E239"),sQuery(id+"F0.wireOp",EDGE,"E240"),sQuery(id+"F0.wireOp",EDGE,"E242"),sQuery(id+"F0.wireOp",EDGE,"E243"),sQuery(id+"F0.wireOp",EDGE,"E244"),sQuery(id+"F0.wireOp",EDGE,"E245"),sQuery(id+"F0.wireOp",EDGE,"E246"),sQuery(id+"F0.wireOp",EDGE,"E247"),sQuery(id+"F0.wireOp",EDGE,"E248"),sQuery(id+"F0.wireOp",EDGE,"E249"),sQuery(id+"F0.wireOp",EDGE,"E250"),sQuery(id+"F0.wireOp",EDGE,"E251"),sQuery(id+"F0.wireOp",EDGE,"E252"),sQuery(id+"F0.wireOp",EDGE,"E253"),sQuery(id+"F0.wireOp",EDGE,"E254"),sQuery(id+"F0.wireOp",EDGE,"E255"),sQuery(id+"F0.wireOp",EDGE,"E256"),sQuery(id+"F0.wireOp",EDGE,"E257"),sQuery(id+"F0.wireOp",EDGE,"E258"),sQuery(id+"F0.wireOp",EDGE,"E259"),sQuery(id+"F0.wireOp",EDGE,"E260"),sQuery(id+"F0.wireOp",EDGE,"E261"),sQuery(id+"F0.wireOp",EDGE,"E262"),sQuery(id+"F0.wireOp",EDGE,"E263"),sQuery(id+"F0.wireOp",EDGE,"E264"),sQuery(id+"F0.wireOp",EDGE,"E265"),sQuery(id+"F0.wireOp",EDGE,"E266"),sQuery(id+"F0.wireOp",EDGE,"E267"),sQuery(id+"F0.wireOp",EDGE,"E268"),sQuery(id+"F0.wireOp",EDGE,"E269"),sQuery(id+"F0.wireOp",EDGE,"E270"),sQuery(id+"F0.wireOp",EDGE,"E271"),sQuery(id+"F0.wireOp",EDGE,"E272"),sQuery(id+"F0.wireOp",EDGE,"E273"),sQuery(id+"F0.wireOp",EDGE,"E274"),sQuery(id+"F0.wireOp",EDGE,"E275"),sQuery(id+"F0.wireOp",EDGE,"E276"),sQuery(id+"F0.wireOp",EDGE,"E277"),sQuery(id+"F0.wireOp",EDGE,"E278"),sQuery(id+"F0.wireOp",EDGE,"E279"),sQuery(id+"F0.wireOp",EDGE,"E280"),sQuery(id+"F0.wireOp",EDGE,"E281"),sQuery(id+"F0.wireOp",EDGE,"E282"),sQuery(id+"F0.wireOp",EDGE,"E283"),sQuery(id+"F0.wireOp",EDGE,"E284"),sQuery(id+"F0.wireOp",EDGE,"E285"),sQuery(id+"F0.wireOp",EDGE,"E286"),sQuery(id+"F0.wireOp",EDGE,"E287"),sQuery(id+"F0.wireOp",EDGE,"E288"),sQuery(id+"F0.wireOp",EDGE,"E289"),sQuery(id+"F0.wireOp",EDGE,"E290"),sQuery(id+"F0.wireOp",EDGE,"E291"),sQuery(id+"F0.wireOp",EDGE,"E292"),sQuery(id+"F0.wireOp",EDGE,"E293"),sQuery(id+"F0.wireOp",EDGE,"E294"),sQuery(id+"F0.wireOp",EDGE,"E295"),sQuery(id+"F0.wireOp",EDGE,"E296"),sQuery(id+"F0.wireOp",EDGE,"E297"),sQuery(id+"F0.wireOp",EDGE,"E299"),sQuery(id+"F0.wireOp",EDGE,"E300"),sQuery(id+"F0.wireOp",EDGE,"E301"),sQuery(id+"F0.wireOp",EDGE,"E302"),sQuery(id+"F0.wireOp",EDGE,"E303"),sQuery(id+"F0.wireOp",EDGE,"E304"),sQuery(id+"F0.wireOp",EDGE,"E305"),sQuery(id+"F0.wireOp",EDGE,"E306"),sQuery(id+"F0.wireOp",EDGE,"E307"),sQuery(id+"F0.wireOp",EDGE,"E310"),sQuery(id+"F0.wireOp",EDGE,"E311"),sQuery(id+"F0.wireOp",EDGE,"E313"),sQuery(id+"F0.wireOp",EDGE,"E314"),sQuery(id+"F0.wireOp",EDGE,"E316"),sQuery(id+"F0.wireOp",EDGE,"E317"),sQuery(id+"F0.wireOp",EDGE,"E318"),sQuery(id+"F0.wireOp",EDGE,"E319"),sQuery(id+"F0.wireOp",EDGE,"E320"),sQuery(id+"F0.wireOp",EDGE,"E321"),sQuery(id+"F0.wireOp",EDGE,"E322"),sQuery(id+"F0.wireOp",EDGE,"E323"),sQuery(id+"F0.wireOp",EDGE,"E325"),sQuery(id+"F0.wireOp",EDGE,"E326"),sQuery(id+"F0.wireOp",EDGE,"E327"),sQuery(id+"F0.wireOp",EDGE,"E328"),sQuery(id+"F0.wireOp",EDGE,"E329"),sQuery(id+"F0.wireOp",EDGE,"E330"),sQuery(id+"F0.wireOp",EDGE,"E331"),sQuery(id+"F0.wireOp",EDGE,"E332"),sQuery(id+"F0.wireOp",EDGE,"E333"),sQuery(id+"F0.wireOp",EDGE,"E336"),sQuery(id+"F0.wireOp",EDGE,"E337"),sQuery(id+"F0.wireOp",EDGE,"E338"),sQuery(id+"F0.wireOp",EDGE,"E339"),sQuery(id+"F0.wireOp",EDGE,"E340"),sQuery(id+"F0.wireOp",EDGE,"E341"),sQuery(id+"F0.wireOp",EDGE,"E342"),sQuery(id+"F0.wireOp",EDGE,"E343"),sQuery(id+"F0.wireOp",EDGE,"E345"),sQuery(id+"F0.wireOp",EDGE,"E347"),sQuery(id+"F0.wireOp",EDGE,"E350"),sQuery(id+"F0.wireOp",EDGE,"E351"),sQuery(id+"F0.wireOp",EDGE,"E352"),sQuery(id+"F0.wireOp",EDGE,"E353"),sQuery(id+"F0.wireOp",EDGE,"E354"),sQuery(id+"F0.wireOp",EDGE,"E355"),sQuery(id+"F0.wireOp",EDGE,"E356"),sQuery(id+"F0.wireOp",EDGE,"E357"),sQuery(id+"F0.wireOp",EDGE,"E358"),sQuery(id+"F0.wireOp",EDGE,"E359"),sQuery(id+"F0.wireOp",EDGE,"E360"),sQuery(id+"F0.wireOp",EDGE,"E361"),sQuery(id+"F0.wireOp",EDGE,"E363"),sQuery(id+"F0.wireOp",EDGE,"E364"),sQuery(id+"F0.wireOp",EDGE,"E365"),sQuery(id+"F0.wireOp",EDGE,"E367"),sQuery(id+"F0.wireOp",EDGE,"E369"),sQuery(id+"F0.wireOp",EDGE,"E370")])]});
            var Q1;
            Q1=qCreatedBy(makeId("Origin.pointOp"),VERTEX);
            transform(context, id + "F2", {"entities" : qUnion([Q0]), "transformType" : TransformType.SCALE_UNIFORMLY, "scale" : 2.6, "scalePoint" : qUnion([Q1]), "makeCopy" : false});
        }
    });
